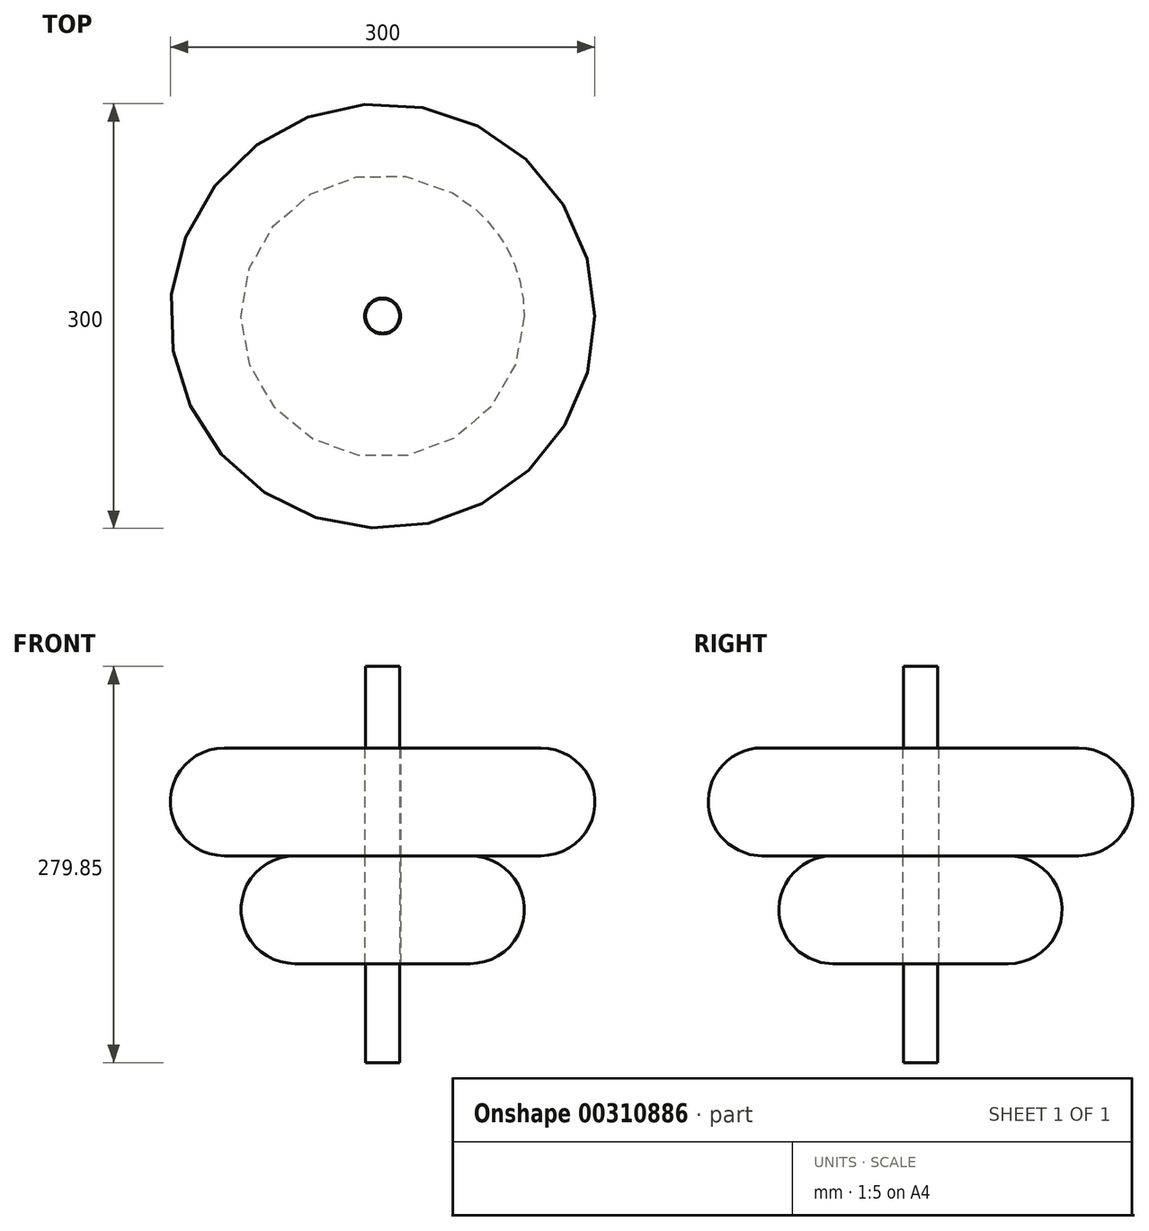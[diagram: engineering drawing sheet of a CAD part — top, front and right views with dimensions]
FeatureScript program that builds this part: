
annotation { "Feature Type Name" : "Feature", "Feature Type Description" : "" }
export const myFeature = defineFeature(function(context is Context, id is Id, definition is map)
    precondition{}
    {
        {
            var Q0;
            Q0=qCreatedBy(makeId("Top.planeOp"),FACE);
            var sketch = newSketch(context, id + "F0", { "sketchPlane" : qUnion([Q0])});
            skCircle(sketch, "E0", {"center": v(0, 0) * mm, "radius": 12.7 * mm});
            skCircle(sketch, "E1", {"center": v(0, 0) * mm, "radius": 100 * mm});
            skCircle(sketch, "E2", {"center": v(0, 0) * mm, "radius": 12.07 * mm});
            skSolve(sketch);
        }
        {
            var Q0;
            Q0 = qSketchRegion(id + "F0", true);
            extrude(context, id + "F1", {"entities" : qUnion([Q0]), "depth" : 76.2 * mm});
        }
        {
            var Q0;
            Q0=makeQuery(id+"F1.opExtrude","CAP_FACE",FACE,{"disambiguationData":[OSD([sQuery(id+"F0.wireOp",EDGE,"E0"),sQuery(id+"F0.wireOp",EDGE,"E1")])],"isStart":false});
            var sketch = newSketch(context, id + "F2", { "sketchPlane" : qUnion([Q0])});
            skCircle(sketch, "E3", {"center": v(0, 0) * mm, "radius": 150 * mm});
            skSolve(sketch);
        }
        {
            var Q0;
            Q0=makeQuery(id+"F2.imprint","IMPRINT",FACE,{"disambiguationData":[TD([[makeQuery(id+"F2.imprint","IMPRINT",EDGE,{"derivedFrom":sQuery(id+"F2.wireOp",EDGE,"E3")}),1.0]])]});
            var Q1;
            Q1=makeQuery(id+"F2.imprint","IMPRINT",FACE,{"disambiguationData":[TD([[makeQuery(id+"F2.imprint","IMPRINT",EDGE,{"derivedFrom":makeQuery(id+"F1.opExtrude","CAP_EDGE",EDGE,{"disambiguationData":[OSD([sQuery(id+"F0.wireOp",EDGE,"E0")])],"isStart":false})}),-1.0]])]});
            extrude(context, id + "F3", {"entities" : qUnion([Q0, Q1]), "depth" : 76.2 * mm});
        }
        {
            var Q0;
            Q0=makeQuery(id+"F1.opExtrude","SWEPT_FACE",FACE,{"disambiguationData":[OSD([sQuery(id+"F0.wireOp",EDGE,"E1")])]});
            fillet(context, id + "F4", {"entities" : qUnion([Q0]), "radius" : 38.1 * mm, "tangentPropagation" : true, "allowEdgeOverflow" : false});
        }
        {
            var Q0;
            Q0=makeQuery(id+"F3.opExtrude","SWEPT_FACE",FACE,{"disambiguationData":[OSD([sQuery(id+"F2.wireOp",EDGE,"E3")])]});
            fillet(context, id + "F5", {"entities" : qUnion([Q0]), "radius" : 38.1 * mm, "tangentPropagation" : true, "allowEdgeOverflow" : false});
        }
        {
            var Q0;
            Q0=makeQuery(id+"F0.imprint","IMPRINT",FACE,{"disambiguationData":[TD([[makeQuery(id+"F0.imprint","IMPRINT",EDGE,{"derivedFrom":sQuery(id+"F0.wireOp",EDGE,"E2")}),1.0]])]});
            extrude(context, id + "F6", {"entities" : qUnion([Q0]), "depth" : 210 * mm});
        }
        {
            var Q0;
            Q0=makeQuery(id+"F6.opExtrude","CAP_FACE",FACE,{"disambiguationData":[OSD([sQuery(id+"F0.wireOp",EDGE,"E2")])],"isStart":true});
            extrude(context, id + "F7", {"entities" : qUnion([Q0]), "operationType" : NewBodyOperationType.ADD, "depth" : 69.85 * mm});
        }
    });
